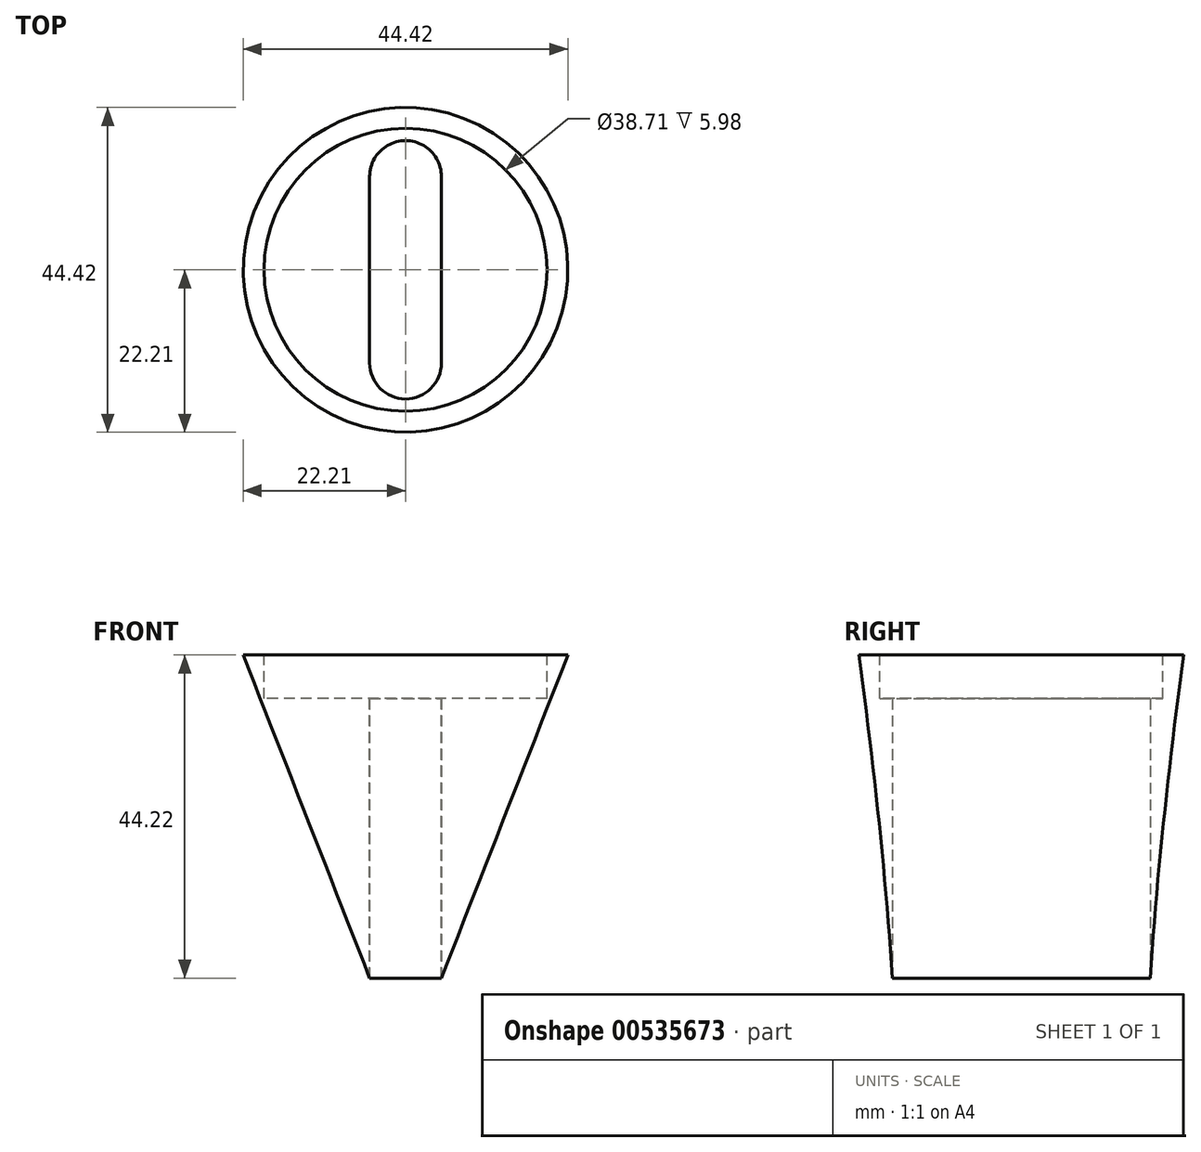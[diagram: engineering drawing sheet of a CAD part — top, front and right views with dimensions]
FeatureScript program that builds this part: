
annotation { "Feature Type Name" : "Feature", "Feature Type Description" : "" }
export const myFeature = defineFeature(function(context is Context, id is Id, definition is map)
    precondition{}
    {
        {
            var Q0;
            Q0=qCreatedBy(makeId("Top.planeOp"),FACE);
            var sketch = newSketch(context, id + "F0", { "sketchPlane" : qUnion([Q0])});
            skCircle(sketch, "E0", {"center": v(0, 0) * mm, "radius": 22.21 * mm});
            skSolve(sketch);
        }
        {
            var Q0;
            Q0=qCreatedBy(makeId("Top.planeOp"),FACE);
            cPlane(context, id + "F1", {"entities" : qUnion([Q0]), "cplaneType" : CPlaneType.OFFSET, "offset" : 44.22 * mm, "oppositeDirection" : true, "width" : 152.4 * mm, "height" : 152.4 * mm});
        }
        {
            var Q0;
            Q0=qCreatedBy(id+"F1.planeOp",FACE);
            var sketch = newSketch(context, id + "F2", { "sketchPlane" : qUnion([Q0])});
            skLineSegment(sketch, "E1.bottom", {"start": v(4.9, 12.77) * mm, "end": v(-4.9, 12.77) * mm});
            skLineSegment(sketch, "E1.top", {"start": v(4.9, -12.77) * mm, "end": v(-4.9, -12.77) * mm});
            skLineSegment(sketch, "E1.left", {"start": v(4.9, 12.77) * mm, "end": v(4.9, -12.77) * mm});
            skLineSegment(sketch, "E1.right", {"start": v(-4.9, 12.77) * mm, "end": v(-4.9, -12.77) * mm});
            skPoint(sketch, "E1.middle", {"position": v(0, 0) * mm});
            skArc(sketch, "E2", {"start": v(-4.9, -12.77) * mm, "mid": v(0, -17.68) * mm, "end": v(4.9, -12.77) * mm});
            skArc(sketch, "E3", {"start": v(4.9, 12.77) * mm, "mid": v(0, 17.68) * mm, "end": v(-4.9, 12.77) * mm});
            skSolve(sketch);
        }
        {
            var Q0;
            Q0 = qSketchRegion(id + "F0", true);
            var Q1;
            Q1 = qSketchRegion(id + "F2", true);
            loft(context, id + "F3", {"sheetProfilesArray" : [{ "sheetProfileEntities" : qUnion([Q0]) }, { "sheetProfileEntities" : qUnion([Q1]) }]});
        }
        {
            var Q0;
            Q0=makeQuery(id+"F3.opLoft","CAP_FACE",FACE,{"disambiguationData":[OSD([makeQuery(id+"F2.imprint","IMPRINT",FACE,{"disambiguationData":[TD([[makeQuery(id+"F2.imprint","IMPRINT",EDGE,{"derivedFrom":sQuery(id+"F2.wireOp",EDGE,"E1.bottom")}),1.0]])]})])],"isStart":true});
            var sketch = newSketch(context, id + "F4", { "sketchPlane" : qUnion([Q0])});
            skLineSegment(sketch, "E4.bottom", {"start": v(4.9, -12.77) * mm, "end": v(-4.9, -12.77) * mm});
            skLineSegment(sketch, "E4.top", {"start": v(4.9, 12.77) * mm, "end": v(-4.9, 12.77) * mm});
            skLineSegment(sketch, "E4.left", {"start": v(4.9, -12.77) * mm, "end": v(4.9, 12.77) * mm});
            skLineSegment(sketch, "E4.right", {"start": v(-4.9, -12.77) * mm, "end": v(-4.9, 12.77) * mm});
            skPoint(sketch, "E4.middle", {"position": v(0, 0) * mm});
            skArc(sketch, "E5", {"start": v(4.9, 12.77) * mm, "mid": v(0, 17.68) * mm, "end": v(-4.9, 12.77) * mm});
            skArc(sketch, "E6", {"start": v(-4.9, -12.77) * mm, "mid": v(0, -17.68) * mm, "end": v(4.9, -12.77) * mm});
            skSolve(sketch);
        }
        {
            var Q0;
            Q0 = qSketchRegion(id + "F4", true);
            extrude(context, id + "F5", {"entities" : qUnion([Q0]), "operationType" : NewBodyOperationType.REMOVE, "oppositeDirection" : true, "depth" : 73 * mm, "offsetDistance" : 25.4 * mm});
        }
        {
            var Q0;
            Q0=makeQuery(id+"F3.opLoft","CAP_FACE",FACE,{"disambiguationData":[OSD([makeQuery(id+"F0.imprint","IMPRINT",FACE,{"disambiguationData":[TD([[makeQuery(id+"F0.imprint","IMPRINT",EDGE,{"derivedFrom":sQuery(id+"F0.wireOp",EDGE,"E0")}),1.0]])]})])],"isStart":true});
            var sketch = newSketch(context, id + "F6", { "sketchPlane" : qUnion([Q0])});
            skCircle(sketch, "E7", {"center": v(0, 0) * mm, "radius": 19.36 * mm});
            skSolve(sketch);
        }
        {
            var Q0;
            Q0 = qSketchRegion(id + "F6", true);
            extrude(context, id + "F7", {"entities" : qUnion([Q0]), "operationType" : NewBodyOperationType.REMOVE, "oppositeDirection" : true, "depth" : 5.98 * mm, "offsetDistance" : 25.4 * mm});
        }
    });
